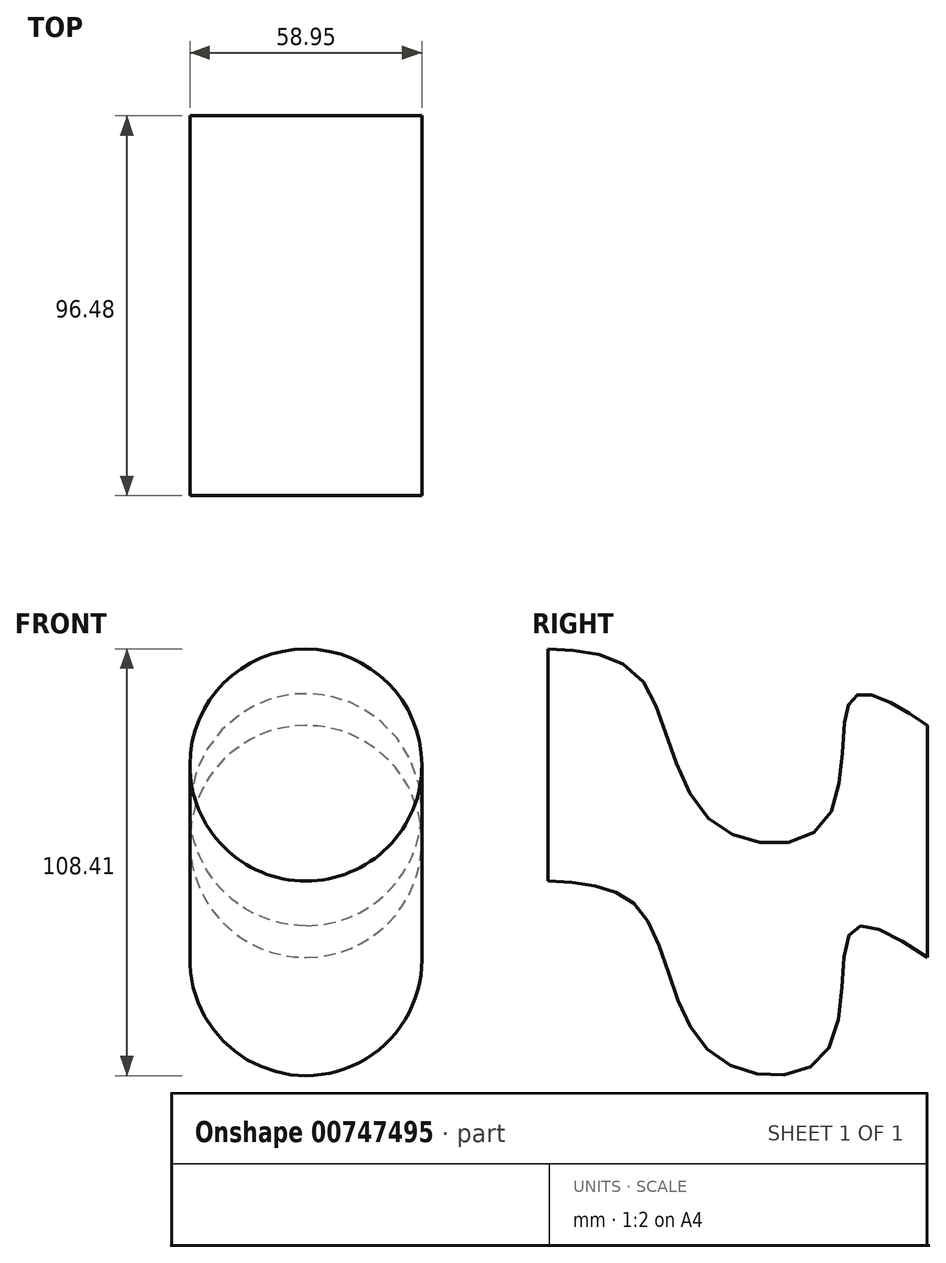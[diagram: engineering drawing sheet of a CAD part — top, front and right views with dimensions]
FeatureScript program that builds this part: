
annotation { "Feature Type Name" : "Feature", "Feature Type Description" : "" }
export const myFeature = defineFeature(function(context is Context, id is Id, definition is map)
    precondition{}
    {
        {
            var Q0;
            Q0=qCreatedBy(makeId("Front.planeOp"),FACE);
            var sketch = newSketch(context, id + "F0", { "sketchPlane" : qUnion([Q0])});
            skCircle(sketch, "E0", {"center": v(-18.32, 15.24) * mm, "radius": 29.47 * mm});
            skSolve(sketch);
        }
        {
            var Q0;
            Q0=qCreatedBy(makeId("Right.planeOp"),FACE);
            var sketch = newSketch(context, id + "F1", { "sketchPlane" : qUnion([Q0])});
            skFitSpline(sketch, "E1", {"points": [v(36.5, -22.93) * mm, v(17.31, -16.03) * mm, v(10.55, -47.26) * mm, v(-18.95, -46.69) * mm, v(-36.32, -11.1) * mm, v(-60, -3.5) * mm], "startDerivative": vector(-142.73, 93.48) * mm, "endDerivative": vector(-147.8, 7.8) * mm});
            skSolve(sketch);
        }
        {
            var Q0;
            Q0=makeQuery(id+"F0.imprint","IMPRINT",FACE,{"disambiguationData":[TD([[makeQuery(id+"F0.imprint","IMPRINT",EDGE,{"derivedFrom":sQuery(id+"F0.wireOp",EDGE,"E0")}),1.0]])]});
            var Q1;
            Q1=sQuery(id+"F1.wireOp",EDGE,"E1");
            sweep(context, id + "F2", {"profiles" : qUnion([Q0]), "path" : qUnion([Q1]), "keepProfileOrientation" : true});
        }
    });
